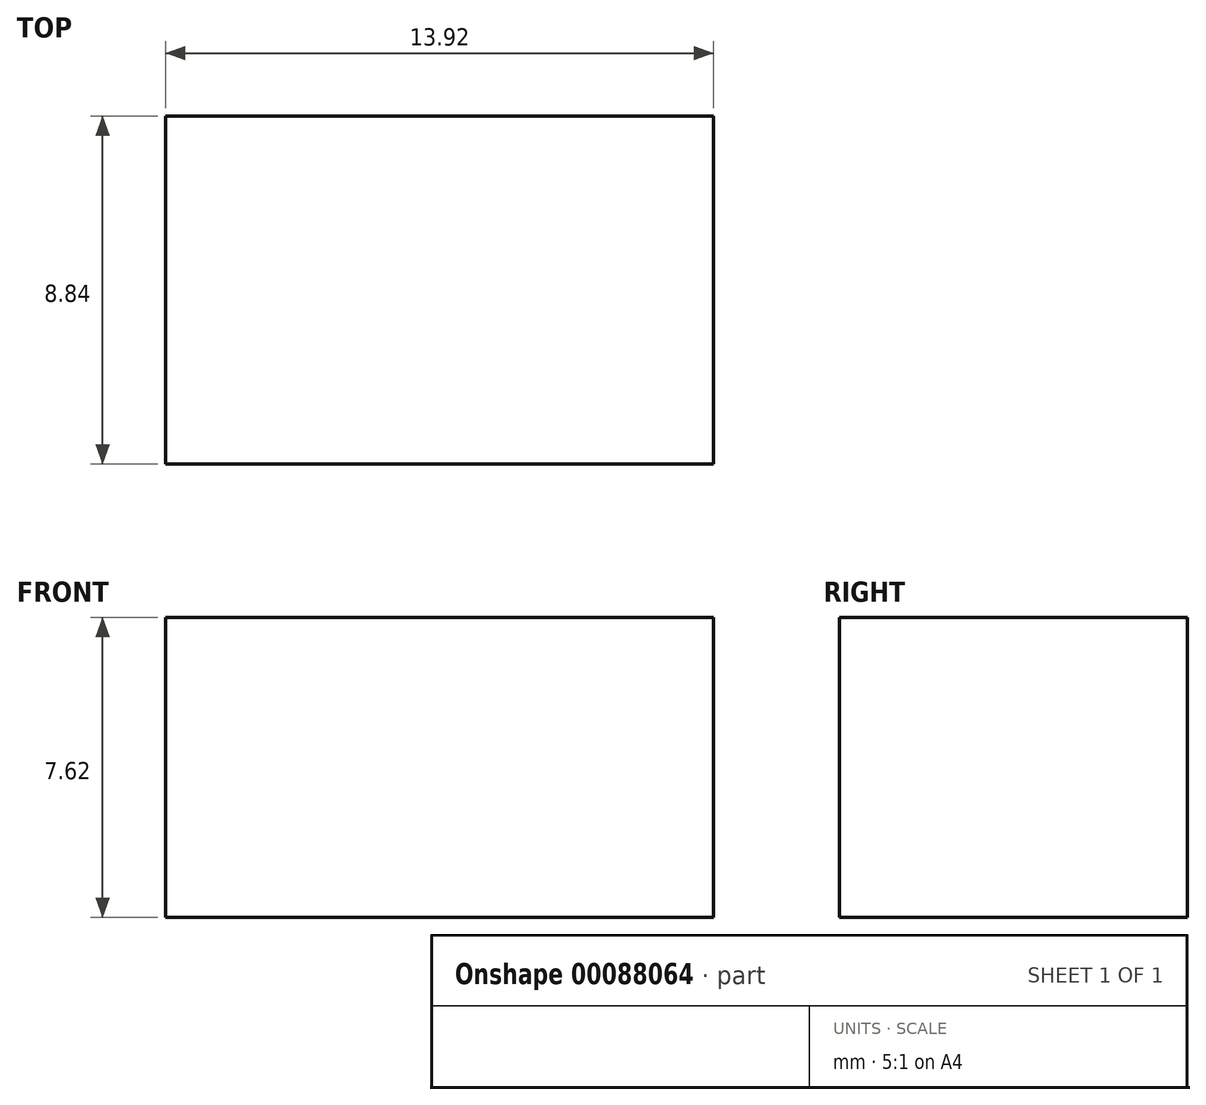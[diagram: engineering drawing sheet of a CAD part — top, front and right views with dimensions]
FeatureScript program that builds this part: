
annotation { "Feature Type Name" : "Feature", "Feature Type Description" : "" }
export const myFeature = defineFeature(function(context is Context, id is Id, definition is map)
    precondition{}
    {
        {
            var Q0;
            Q0=qCreatedBy(makeId("Top.planeOp"),FACE);
            var sketch = newSketch(context, id + "F0", { "sketchPlane" : qUnion([Q0])});
            skLineSegment(sketch, "E0.bottom", {"start": v(6.96, -4.42) * mm, "end": v(-6.96, -4.42) * mm});
            skLineSegment(sketch, "E0.top", {"start": v(6.96, 4.42) * mm, "end": v(-6.96, 4.42) * mm});
            skLineSegment(sketch, "E0.left", {"start": v(6.96, -4.42) * mm, "end": v(6.96, 4.42) * mm});
            skLineSegment(sketch, "E0.right", {"start": v(-6.96, -4.42) * mm, "end": v(-6.96, 4.42) * mm});
            skPoint(sketch, "E0.middle", {"position": v(0, 0) * mm});
            skSolve(sketch);
        }
        {
            var Q0;
            Q0=makeQuery(id+"F0.imprint","IMPRINT",FACE,{"disambiguationData":[TD([[makeQuery(id+"F0.imprint","IMPRINT",EDGE,{"derivedFrom":sQuery(id+"F0.wireOp",EDGE,"E0.bottom")}),-1.0]])]});
            extrude(context, id + "F1", {"entities" : qUnion([Q0]), "depth" : 7.62 * mm});
        }
    });
